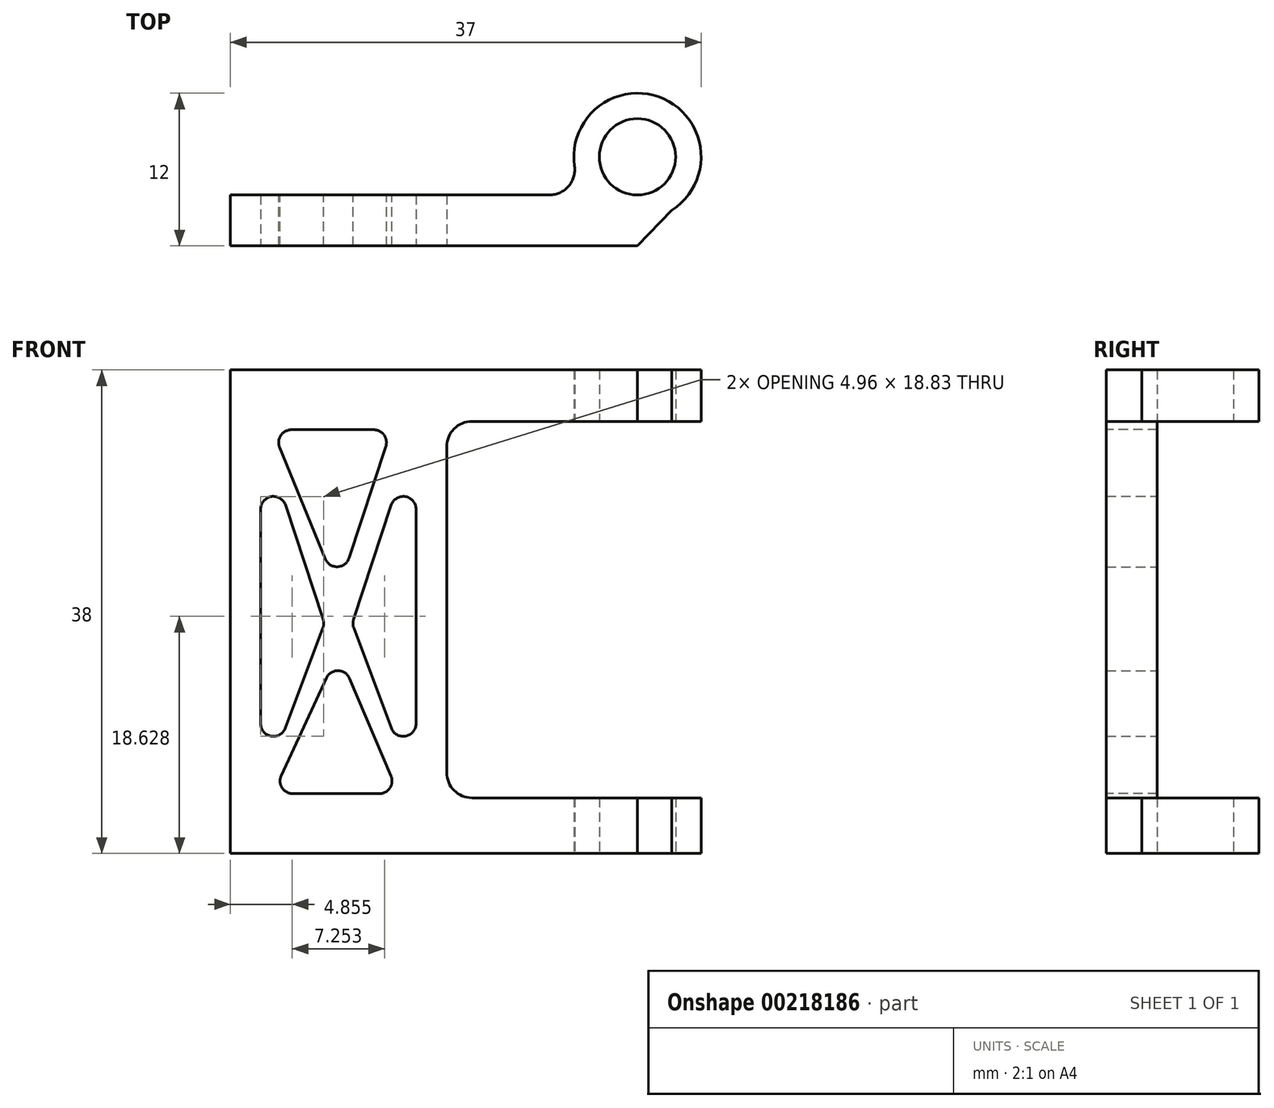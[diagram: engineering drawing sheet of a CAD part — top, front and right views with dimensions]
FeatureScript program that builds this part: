
annotation { "Feature Type Name" : "Feature", "Feature Type Description" : "" }
export const myFeature = defineFeature(function(context is Context, id is Id, definition is map)
    precondition{}
    {
        {
            var Q0;
            Q0=qCreatedBy(makeId("Top.planeOp"),FACE);
            var sketch = newSketch(context, id + "F0", { "sketchPlane" : qUnion([Q0])});
            skArc(sketch, "E0", {"start": v(17.02, 0) * mm, "mid": v(20.3, 8.78) * mm, "end": v(12.07, 4.29) * mm});
            skCircle(sketch, "E1", {"center": v(17.02, 5) * mm, "radius": 3 * mm});
            skLineSegment(sketch, "E2.bottom", {"start": v(17.02, 0) * mm, "end": v(-30.02, 0) * mm});
            skLineSegment(sketch, "E2.top", {"start": v(10.1, 2) * mm, "end": v(-30.02, 2) * mm});
            skLineSegment(sketch, "E2.right", {"start": v(-30.02, 0) * mm, "end": v(-30.02, 2) * mm});
            skPoint(sketch, "E3.visualSharp", {"position": v(13.02, 2) * mm});
            skArc(sketch, "E3.filletArc", {"start": v(10.1, 2) * mm, "mid": v(11.6, 2.7) * mm, "end": v(12.07, 4.29) * mm});
            skSolve(sketch);
        }
        {
            var Q0;
            Q0=qSketchRegion(id+"F0",true);
            extrude(context, id + "F1", {"entities" : qUnion([Q0]), "depth" : 38 * mm});
        }
        {
            var Q0;
            Q0=makeQuery(id+"F1.opExtrude","SWEPT_FACE",FACE,{"disambiguationData":[OSD([sQuery(id+"F0.wireOp",EDGE,"E2.bottom")])]});
            var sketch = newSketch(context, id + "F2", { "sketchPlane" : qUnion([Q0])});
            skLineSegment(sketch, "E4.bottom", {"start": v(-30.02, 33.5) * mm, "end": v(-16.98, 33.5) * mm});
            skLineSegment(sketch, "E4.top", {"start": v(-30.02, 4.5) * mm, "end": v(-16.98, 4.5) * mm});
            skLineSegment(sketch, "E4.left", {"start": v(-30.02, 33.5) * mm, "end": v(-30.02, 4.5) * mm});
            skLineSegment(sketch, "E4.right", {"start": v(-14.98, 31.5) * mm, "end": v(-14.98, 6.5) * mm});
            skLineSegment(sketch, "E5.bottom", {"start": v(38.1, 33.96) * mm, "end": v(4.02, 33.96) * mm});
            skLineSegment(sketch, "E5.top", {"start": v(38.1, 4.37) * mm, "end": v(4.02, 4.37) * mm});
            skLineSegment(sketch, "E5.left", {"start": v(38.1, 33.96) * mm, "end": v(38.1, 4.37) * mm});
            skLineSegment(sketch, "E5.right", {"start": v(2.02, 31.96) * mm, "end": v(2.02, 6.37) * mm});
            skPoint(sketch, "E6", {"position": v(-30.02, 19) * mm});
            skPoint(sketch, "E7.visualSharp", {"position": v(-14.98, 33.5) * mm});
            skArc(sketch, "E7.filletArc", {"start": v(-14.98, 31.5) * mm, "mid": v(-15.57, 32.91) * mm, "end": v(-16.98, 33.5) * mm});
            skPoint(sketch, "E8.visualSharp", {"position": v(-14.98, 4.5) * mm});
            skArc(sketch, "E8.filletArc", {"start": v(-16.98, 4.5) * mm, "mid": v(-15.57, 5.09) * mm, "end": v(-14.98, 6.5) * mm});
            skPoint(sketch, "E9.visualSharp", {"position": v(2.02, 33.96) * mm});
            skArc(sketch, "E9.filletArc", {"start": v(4.02, 33.96) * mm, "mid": v(2.6, 33.37) * mm, "end": v(2.02, 31.96) * mm});
            skPoint(sketch, "E10.visualSharp", {"position": v(2.02, 4.37) * mm});
            skArc(sketch, "E10.filletArc", {"start": v(2.02, 6.37) * mm, "mid": v(2.6, 4.95) * mm, "end": v(4.02, 4.37) * mm});
            skSolve(sketch);
        }
        {
            var Q0;
            Q0=makeQuery(id+"F1.opExtrude","SWEPT_FACE",FACE,{"disambiguationData":[OSD([sQuery(id+"F0.wireOp",EDGE,"E2.bottom")])]});
            var sketch = newSketch(context, id + "F3", { "sketchPlane" : qUnion([Q0])});
            skSolve(sketch);
        }
        {
            var Q0;
            {var subQ1=sQuery(id+"F0.wireOp",EDGE,"E2.bottom");Q0=makeQuery(id+"F3.imprint","IMPRINT",FACE,{"disambiguationData":[TD([[makeQuery(id+"F3.imprint","IMPRINT",EDGE,{"derivedFrom":makeQuery(id+"F1.opExtrude","CAP_EDGE",EDGE,{"disambiguationData":[OSD([subQ1])],"isStart":true})}),-1.0]])]});}
            extrude(context, id + "F4", {"entities" : qUnion([Q0]), "operationType" : NewBodyOperationType.ADD, "depth" : 2 * mm});
        }
        {
            var Q0;
            {var subQ0=sQuery(id+"F0.wireOp",EDGE,"E2.bottom");Q0=makeQuery(id+"F4.boolean.opBoolean","MERGE",FACE,{"derivedFrom":[makeQuery(id+"F1.opExtrude","CAP_FACE",FACE,{"disambiguationData":[OSD([sQuery(id+"F0.wireOp",EDGE,"E0"),sQuery(id+"F0.wireOp",EDGE,"E1"),subQ0,sQuery(id+"F0.wireOp",EDGE,"E2.top"),sQuery(id+"F0.wireOp",EDGE,"E2.right"),sQuery(id+"F0.wireOp",EDGE,"E3.filletArc")])],"isStart":true}),makeQuery(id+"F4.opExtrude","SWEPT_FACE",FACE,{"disambiguationData":[OSD([subQ0]),TDD([makeQuery(id+"F3.imprint","IMPRINT",EDGE,{"derivedFrom":makeQuery(id+"F1.opExtrude","CAP_EDGE",EDGE,{"disambiguationData":[OSD([subQ0])],"isStart":true})})])]})]});}
            var sketch = newSketch(context, id + "F5", { "sketchPlane" : qUnion([Q0])});
            skLineSegment(sketch, "E11", {"start": v(17.02, 2) * mm, "end": v(21.31, -2.44) * mm});
            skLineSegment(sketch, "E12", {"start": v(21.31, -2.44) * mm, "end": v(17.02, 0) * mm});
            skLineSegment(sketch, "E13", {"start": v(17.02, 0) * mm, "end": v(17.02, 2) * mm});
            skSolve(sketch);
        }
        {
            var Q0;
            {var subQ0=sQuery(id+"F5.wireOp",EDGE,"E13");Q0=makeQuery(id+"F5.imprint","IMPRINT",FACE,{"disambiguationData":[TD([[makeQuery(id+"F5.imprint","IMPRINT",EDGE,{"derivedFrom":subQ0}),1.0]])]});}
            extrude(context, id + "F6", {"entities" : qUnion([Q0]), "operationType" : NewBodyOperationType.ADD, "oppositeDirection" : true, "depth" : 38 * mm});
        }
        {
            var Q0;
            Q0 = qSketchRegion(id + "F2", true);
            extrude(context, id + "F7", {"entities" : qUnion([Q0]), "operationType" : NewBodyOperationType.REMOVE, "endBound" : BoundingType.SYMMETRIC, "oppositeDirection" : true, "depth" : 25 * mm});
        }
        {
            var Q0;
            Q0=makeQuery(id+"F4.opExtrude","CAP_FACE",FACE,{"disambiguationData":[OSD([sQuery(id+"F0.wireOp",EDGE,"E0"),sQuery(id+"F0.wireOp",EDGE,"E2.bottom"),sQuery(id+"F0.wireOp",EDGE,"E2.right")])],"isStart":false});
            var sketch = newSketch(context, id + "F8", { "sketchPlane" : qUnion([Q0])});
            skLineSegment(sketch, "E14", {"start": v(-12.6, 33.3) * mm, "end": v(-12.6, 4.7) * mm});
            skLineSegment(sketch, "E15", {"start": v(-12.6, 4.7) * mm, "end": v(-7.59, 18.05) * mm});
            skLineSegment(sketch, "E16", {"start": v(-7.59, 18.05) * mm, "end": v(-12.6, 33.3) * mm});
            skLineSegment(sketch, "E17", {"start": v(-6.5, 38) * mm, "end": v(-6.5, -2.67) * mm, "construction": true});
            skPoint(sketch, "E17.endSnap0", {"position": v(-6.5, 0) * mm});
            skLineSegment(sketch, "E18.MirrorCS", {"start": v(-5.41, 18.05) * mm, "end": v(-0.4, 33.3) * mm});
            skLineSegment(sketch, "E19.MirrorCS", {"start": v(-0.4, 33.3) * mm, "end": v(-0.4, 4.7) * mm});
            skLineSegment(sketch, "E20.MirrorCS", {"start": v(-0.4, 4.7) * mm, "end": v(-5.41, 18.05) * mm});
            skLineSegment(sketch, "E21", {"start": v(-11.68, 33.3) * mm, "end": v(-6.5, 20.64) * mm});
            skLineSegment(sketch, "E22", {"start": v(-6.5, 20.64) * mm, "end": v(-2.33, 33.3) * mm});
            skLineSegment(sketch, "E23", {"start": v(-2.33, 33.3) * mm, "end": v(-11.68, 33.3) * mm});
            skLineSegment(sketch, "E24", {"start": v(-6.5, 15.83) * mm, "end": v(-11.64, 4.7) * mm});
            skLineSegment(sketch, "E25", {"start": v(-11.64, 4.7) * mm, "end": v(-1.77, 4.7) * mm});
            skLineSegment(sketch, "E26", {"start": v(-1.77, 4.7) * mm, "end": v(-6.5, 15.83) * mm});
            skSolve(sketch);
        }
        {
            var Q0;
            Q0 = qSketchRegion(id + "F8", true);
            extrude(context, id + "F9", {"entities" : qUnion([Q0]), "operationType" : NewBodyOperationType.REMOVE, "oppositeDirection" : true, "depth" : 25 * mm});
        }
        {
            var Q0;
            Q0=makeQuery(id+"F9.boolean.opBoolean","COPY",EDGE,{"derivedFrom":makeQuery(id+"F9.opExtrude","SWEPT_EDGE",EDGE,{"disambiguationData":[OSD([sQuery(id+"F8.wireOp",EDGE,"E21"),sQuery(id+"F8.wireOp",EDGE,"E23")])]})});
            var Q1;
            Q1=makeQuery(id+"F9.boolean.opBoolean","COPY",EDGE,{"derivedFrom":makeQuery(id+"F9.opExtrude","SWEPT_EDGE",EDGE,{"disambiguationData":[OSD([sQuery(id+"F8.wireOp",EDGE,"E22"),sQuery(id+"F8.wireOp",EDGE,"E23")])]})});
            var Q2;
            Q2=makeQuery(id+"F9.boolean.opBoolean","COPY",EDGE,{"derivedFrom":makeQuery(id+"F9.opExtrude","SWEPT_EDGE",EDGE,{"disambiguationData":[OSD([sQuery(id+"F8.wireOp",EDGE,"E14"),sQuery(id+"F8.wireOp",EDGE,"E16")])]})});
            var Q3;
            Q3=makeQuery(id+"F9.boolean.opBoolean","COPY",EDGE,{"derivedFrom":makeQuery(id+"F9.opExtrude","SWEPT_EDGE",EDGE,{"disambiguationData":[OSD([sQuery(id+"F8.wireOp",EDGE,"E14"),sQuery(id+"F8.wireOp",EDGE,"E15")])]})});
            var Q4;
            Q4=makeQuery(id+"F9.boolean.opBoolean","COPY",EDGE,{"derivedFrom":makeQuery(id+"F9.opExtrude","SWEPT_EDGE",EDGE,{"disambiguationData":[OSD([sQuery(id+"F8.wireOp",EDGE,"E15"),sQuery(id+"F8.wireOp",EDGE,"E16")])]})});
            var Q5;
            Q5=makeQuery(id+"F9.boolean.opBoolean","COPY",EDGE,{"derivedFrom":makeQuery(id+"F9.opExtrude","SWEPT_EDGE",EDGE,{"disambiguationData":[OSD([sQuery(id+"F8.wireOp",EDGE,"E21"),sQuery(id+"F8.wireOp",EDGE,"E22")])]})});
            var Q6;
            Q6=makeQuery(id+"F9.boolean.opBoolean","COPY",EDGE,{"derivedFrom":makeQuery(id+"F9.opExtrude","SWEPT_EDGE",EDGE,{"disambiguationData":[OSD([sQuery(id+"F8.wireOp",EDGE,"E18.MirrorCS"),sQuery(id+"F8.wireOp",EDGE,"E19.MirrorCS")])]})});
            var Q7;
            Q7=makeQuery(id+"F9.boolean.opBoolean","COPY",EDGE,{"derivedFrom":makeQuery(id+"F9.opExtrude","SWEPT_EDGE",EDGE,{"disambiguationData":[OSD([sQuery(id+"F8.wireOp",EDGE,"E18.MirrorCS"),sQuery(id+"F8.wireOp",EDGE,"E20.MirrorCS")])]})});
            var Q8;
            Q8=makeQuery(id+"F9.boolean.opBoolean","COPY",EDGE,{"derivedFrom":makeQuery(id+"F9.opExtrude","SWEPT_EDGE",EDGE,{"disambiguationData":[OSD([sQuery(id+"F8.wireOp",EDGE,"E19.MirrorCS"),sQuery(id+"F8.wireOp",EDGE,"E20.MirrorCS")])]})});
            var Q9;
            Q9=makeQuery(id+"F9.boolean.opBoolean","COPY",EDGE,{"derivedFrom":makeQuery(id+"F9.opExtrude","SWEPT_EDGE",EDGE,{"disambiguationData":[OSD([sQuery(id+"F8.wireOp",EDGE,"E24"),sQuery(id+"F8.wireOp",EDGE,"E26")])]})});
            var Q10;
            Q10=makeQuery(id+"F9.boolean.opBoolean","COPY",EDGE,{"derivedFrom":makeQuery(id+"F9.opExtrude","SWEPT_EDGE",EDGE,{"disambiguationData":[OSD([sQuery(id+"F8.wireOp",EDGE,"E25"),sQuery(id+"F8.wireOp",EDGE,"E26")])]})});
            var Q11;
            Q11=makeQuery(id+"F9.boolean.opBoolean","COPY",EDGE,{"derivedFrom":makeQuery(id+"F9.opExtrude","SWEPT_EDGE",EDGE,{"disambiguationData":[OSD([sQuery(id+"F8.wireOp",EDGE,"E24"),sQuery(id+"F8.wireOp",EDGE,"E25")])]})});
            fillet(context, id + "F10", {"entities" : qUnion([Q0, Q1, Q2, Q3, Q4, Q5, Q6, Q7, Q8, Q9, Q10, Q11]), "radius" : 1 * mm, "tangentPropagation" : true, "allowEdgeOverflow" : false});
        }
        {
            var Q0;
            Q0=makeQuery(id+"F4.opExtrude","CAP_FACE",FACE,{"disambiguationData":[OSD([sQuery(id+"F0.wireOp",EDGE,"E0"),sQuery(id+"F0.wireOp",EDGE,"E2.bottom"),sQuery(id+"F0.wireOp",EDGE,"E2.right")])],"isStart":false});
            var sketch = newSketch(context, id + "F11", { "sketchPlane" : qUnion([Q0])});
            skLineSegment(sketch, "E27.bottom", {"start": v(-14.98, 42.3) * mm, "end": v(-33.25, 42.3) * mm});
            skLineSegment(sketch, "E27.top", {"start": v(-14.98, -5.24) * mm, "end": v(-33.25, -5.24) * mm});
            skLineSegment(sketch, "E27.left", {"start": v(-14.98, 42.3) * mm, "end": v(-14.98, -5.24) * mm});
            skLineSegment(sketch, "E27.right", {"start": v(-33.25, 42.3) * mm, "end": v(-33.25, -5.24) * mm});
            skSolve(sketch);
        }
        {
            var Q0;
            Q0 = qSketchRegion(id + "F11", true);
            extrude(context, id + "F12", {"entities" : qUnion([Q0]), "operationType" : NewBodyOperationType.REMOVE, "oppositeDirection" : true, "depth" : 25 * mm});
        }
    });
